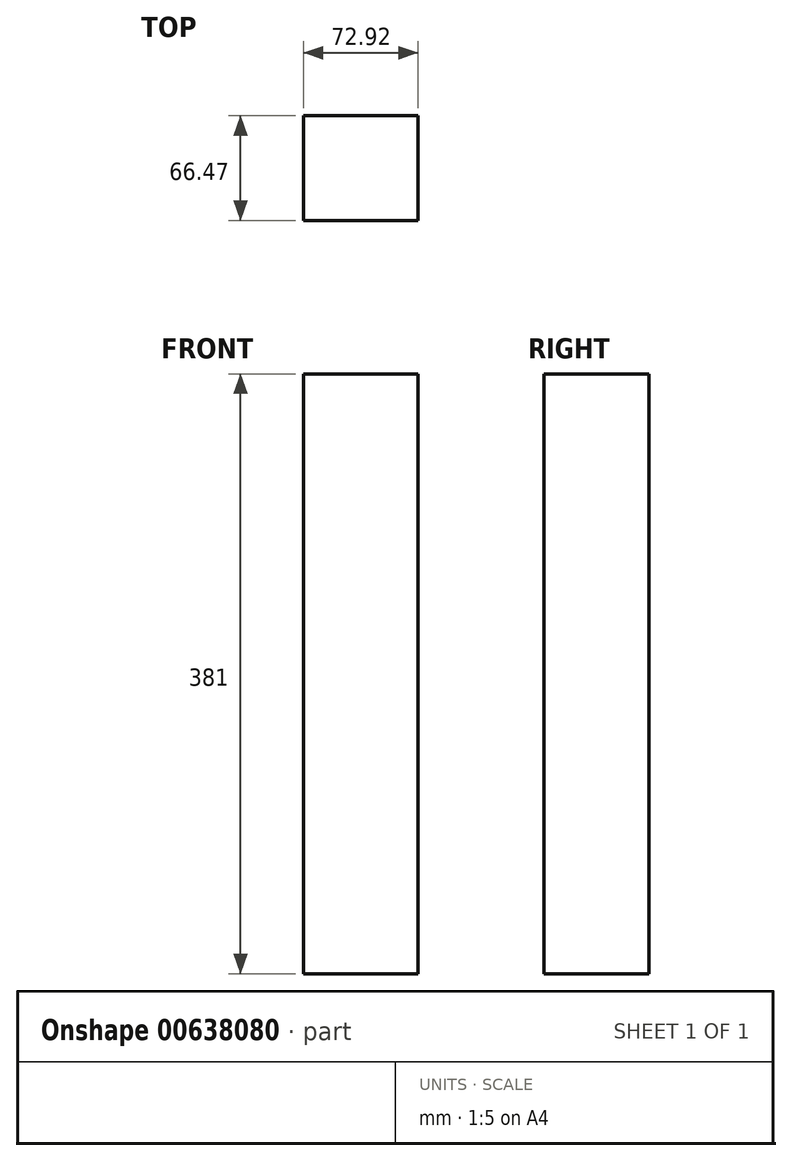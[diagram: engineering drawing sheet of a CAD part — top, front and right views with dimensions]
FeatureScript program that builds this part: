
annotation { "Feature Type Name" : "Feature", "Feature Type Description" : "" }
export const myFeature = defineFeature(function(context is Context, id is Id, definition is map)
    precondition{}
    {
        {
            var Q0;
            Q0=qCreatedBy(makeId("Top.planeOp"),FACE);
            var sketch = newSketch(context, id + "F0", { "sketchPlane" : qUnion([Q0])});
            skLineSegment(sketch, "E0.bottom", {"start": v(-36.28, 26.76) * mm, "end": v(36.64, 26.76) * mm});
            skLineSegment(sketch, "E0.top", {"start": v(-36.28, -39.71) * mm, "end": v(36.64, -39.71) * mm});
            skLineSegment(sketch, "E0.left", {"start": v(-36.28, 26.76) * mm, "end": v(-36.28, -39.71) * mm});
            skLineSegment(sketch, "E0.right", {"start": v(36.64, 26.76) * mm, "end": v(36.64, -39.71) * mm});
            skSolve(sketch);
        }
        {
            var Q0;
            Q0 = qSketchRegion(id + "F0", true);
            extrude(context, id + "F1", {"entities" : qUnion([Q0]), "depth" : 381 * mm, "offsetDistance" : 25.4 * mm});
        }
    });
